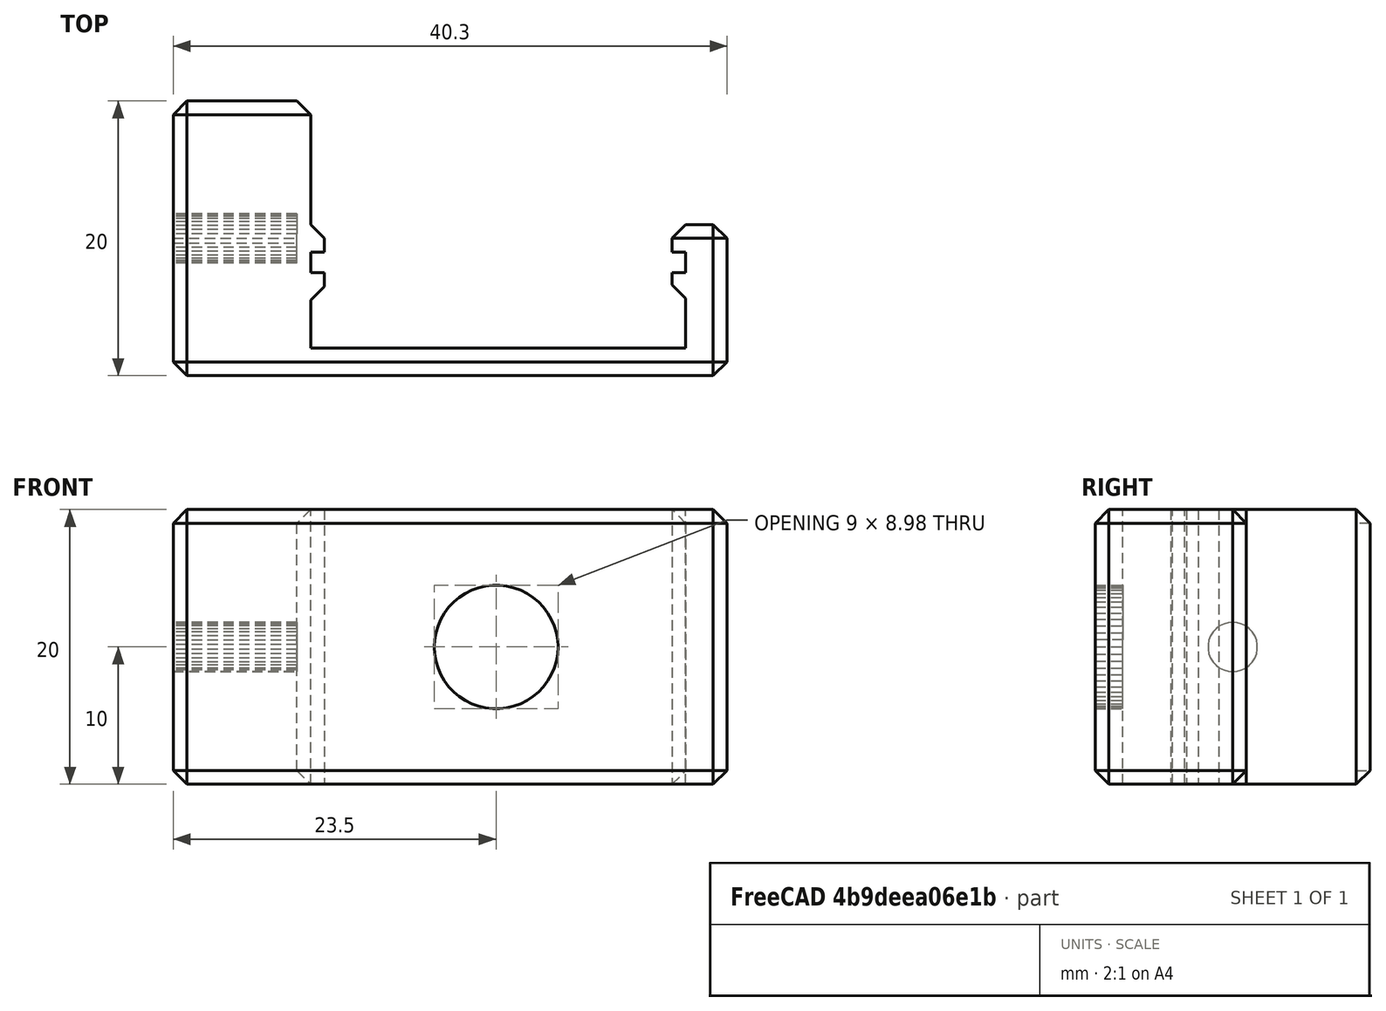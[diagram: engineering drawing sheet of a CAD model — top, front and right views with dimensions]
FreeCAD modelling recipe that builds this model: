
FCSTD DOCUMENT  (FreeCAD 0.20R29177 +426 (Git))
Label: esp32camMountRefined
License: All rights reserved
LicenseURL: http://en.wikipedia.org/wiki/All_rights_reserved
objects: Part::Feature×2, Mesh::Feature×1, Part::Refine×1, PartDesign::FeatureBase×1, PartDesign::CoordinateSystem×1, PartDesign::Body×1
note: 6 computed .brp shape members not serialized (recipe doc carries the construction recipe); baked Part::Feature solids carry a one-line shape summary decoded from their .brp

FEATURE [Mesh::Feature] ImageToStl_com_esp_32_cam_mount  label="ImageToStl.com_esp+32+cam+mount"
  Placement = pos=(-52,-21,0) rot=(0,0,1;0rad)
FEATURE [Part::Feature] ImageToStl_com_esp_32_cam_mount001
  shape: bbox 40.3 x 20 x 20 mm, 552 faces, 0 solids (baked)
FEATURE [Part::Refine] ImageToStl_com_esp_32_cam_mount001001
  Source = -> ImageToStl_com_esp_32_cam_mount001
FEATURE [Part::Feature] ImageToStl_com_esp_32_cam_mount001001_solid  label="ImageToStl_com_esp_32_cam_mount001001 (Solid)"
  shape: bbox 40.3 x 20 x 20 mm, 137 faces (baked)
FEATURE [PartDesign::FeatureBase] BaseFeature
  BaseFeature = -> ImageToStl_com_esp_32_cam_mount001001_solid
FEATURE [PartDesign::CoordinateSystem] LCS_1
  AttacherType = Attacher::AttachEngine3D
  MapMode = 45
  Placement = pos=(-21,9,10) rot=(0.57735,0.57735,0.57735;2.0944rad)
  Support = -> [BaseFeature]
FEATURE [PartDesign::Body] Body  label="mountBody"
  BaseFeature = -> ImageToStl_com_esp_32_cam_mount001001_solid
  Group = -> [BaseFeature,LCS_1]
  Origin = -> Origin
  Tip = -> BaseFeature
